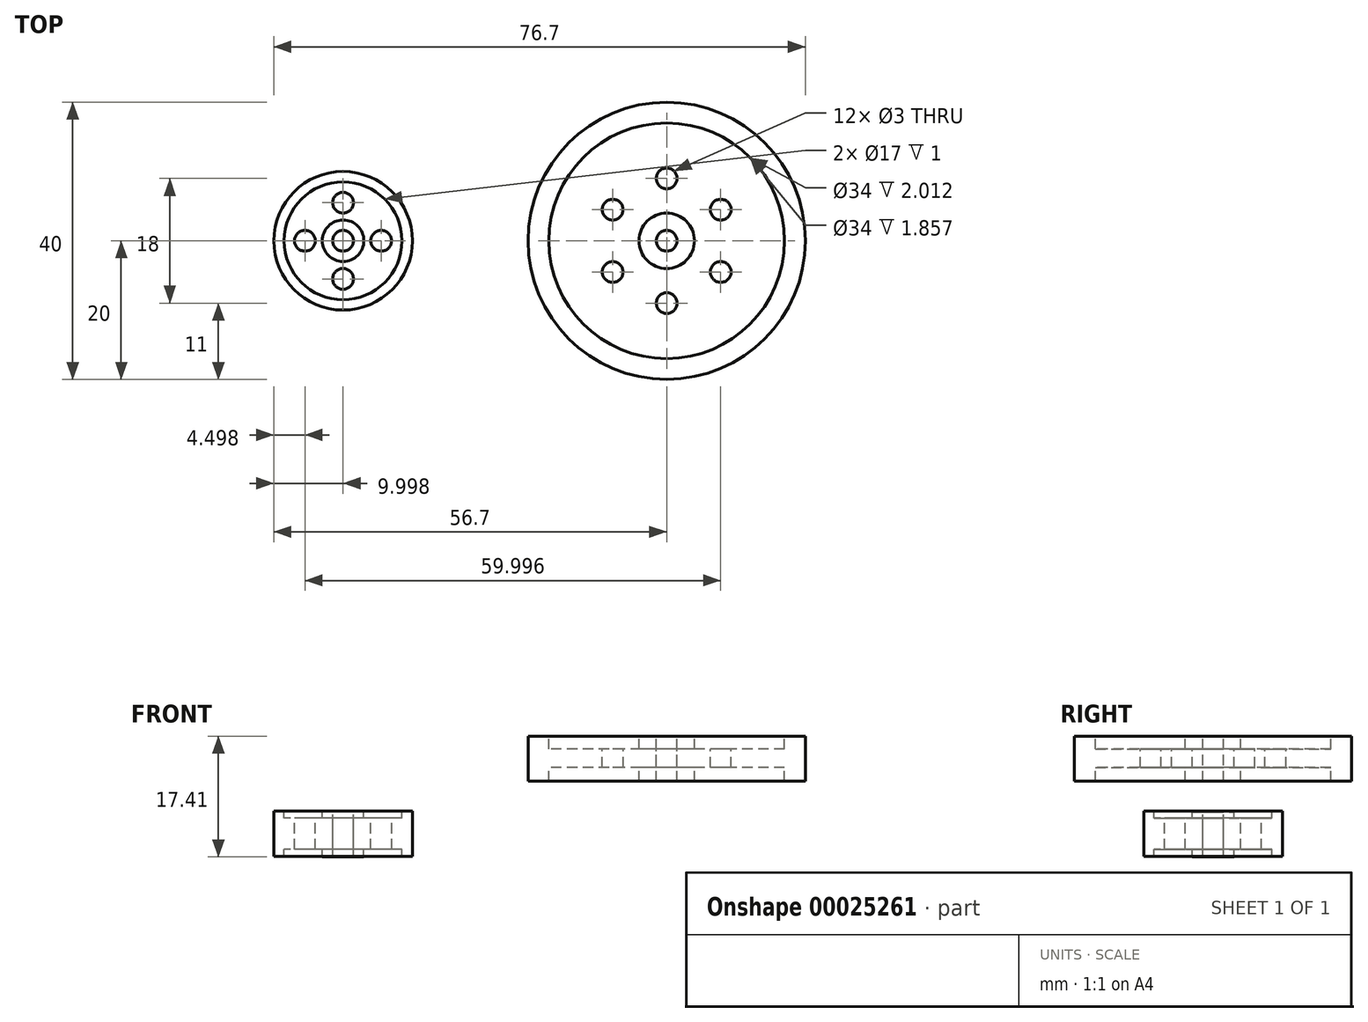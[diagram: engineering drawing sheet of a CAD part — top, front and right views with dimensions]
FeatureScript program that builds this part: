
annotation { "Feature Type Name" : "Feature", "Feature Type Description" : "" }
export const myFeature = defineFeature(function(context is Context, id is Id, definition is map)
    precondition{}
    {
        {
            var Q0;
            Q0=qCreatedBy(makeId("Front.planeOp"),FACE);
            var sketch = newSketch(context, id + "F0", { "sketchPlane" : qUnion([Q0])});
            skLineSegment(sketch, "E0", {"start": v(0, 28.4) * mm, "end": v(0, -27) * mm, "construction": true});
            skLineSegment(sketch, "E1.bottom", {"start": v(1.5, 10.14) * mm, "end": v(4, 10.14) * mm});
            skLineSegment(sketch, "E1.top", {"start": v(1.5, 3.64) * mm, "end": v(4, 3.64) * mm});
            skLineSegment(sketch, "E1.left", {"start": v(1.5, 10.14) * mm, "end": v(1.5, 3.64) * mm});
            skLineSegment(sketch, "E1.right", {"start": v(4, 10.14) * mm, "end": v(4, 3.64) * mm});
            skLineSegment(sketch, "E2.bottom", {"start": v(4, 8.28) * mm, "end": v(17, 8.28) * mm});
            skLineSegment(sketch, "E2.top", {"start": v(4, 5.65) * mm, "end": v(17, 5.65) * mm});
            skLineSegment(sketch, "E2.left", {"start": v(4, 8.28) * mm, "end": v(4, 5.65) * mm});
            skLineSegment(sketch, "E2.right", {"start": v(17, 8.28) * mm, "end": v(17, 5.65) * mm});
            skLineSegment(sketch, "E3.bottom", {"start": v(17, 10.14) * mm, "end": v(20, 10.14) * mm});
            skLineSegment(sketch, "E3.top", {"start": v(17, 3.64) * mm, "end": v(20, 3.64) * mm});
            skLineSegment(sketch, "E3.left", {"start": v(17, 10.14) * mm, "end": v(17, 3.64) * mm});
            skLineSegment(sketch, "E3.right", {"start": v(20, 10.14) * mm, "end": v(20, 3.64) * mm});
            skLineSegment(sketch, "E4", {"start": v(-46.7, 2.05) * mm, "end": v(-46.7, -13.35) * mm, "construction": true});
            skLineSegment(sketch, "E5.bottom", {"start": v(-45.2, -0.77) * mm, "end": v(-43.7, -0.77) * mm});
            skLineSegment(sketch, "E5.top", {"start": v(-45.2, -7.27) * mm, "end": v(-43.7, -7.27) * mm});
            skLineSegment(sketch, "E5.left", {"start": v(-45.2, -0.77) * mm, "end": v(-45.2, -7.27) * mm});
            skLineSegment(sketch, "E5.right", {"start": v(-43.7, -0.77) * mm, "end": v(-43.7, -7.27) * mm});
            skLineSegment(sketch, "E6.bottom", {"start": v(-43.7, -6.19) * mm, "end": v(-38.2, -6.19) * mm});
            skLineSegment(sketch, "E6.top", {"start": v(-43.7, -1.69) * mm, "end": v(-38.2, -1.69) * mm});
            skLineSegment(sketch, "E6.left", {"start": v(-43.7, -1.69) * mm, "end": v(-43.7, -6.19) * mm});
            skLineSegment(sketch, "E6.right", {"start": v(-38.2, -1.69) * mm, "end": v(-38.2, -6.19) * mm});
            skLineSegment(sketch, "E7.bottom", {"start": v(-38.2, -0.69) * mm, "end": v(-36.7, -0.69) * mm});
            skLineSegment(sketch, "E7.top", {"start": v(-38.2, -7.19) * mm, "end": v(-36.7, -7.19) * mm});
            skLineSegment(sketch, "E7.left", {"start": v(-38.2, -0.69) * mm, "end": v(-38.2, -7.19) * mm});
            skLineSegment(sketch, "E7.right", {"start": v(-36.7, -0.69) * mm, "end": v(-36.7, -7.19) * mm});
            skSolve(sketch);
        }
        {
            var Q0;
            {var subQ3=sQuery(id+"F0.wireOp",EDGE,"E1.bottom");Q0=makeQuery(id+"F0.imprint","IMPRINT",FACE,{"disambiguationData":[TD([[makeQuery(id+"F0.imprint","IMPRINT",EDGE,{"derivedFrom":subQ3}),-1.0]])]});}
            var Q1;
            {var subQ4=sQuery(id+"F0.wireOp",EDGE,"E3.bottom");Q1=makeQuery(id+"F0.imprint","IMPRINT",FACE,{"disambiguationData":[TD([[makeQuery(id+"F0.imprint","IMPRINT",EDGE,{"derivedFrom":subQ4}),-1.0]])]});}
            var Q2;
            {var subQ2=sQuery(id+"F0.wireOp",EDGE,"E2.bottom");Q2=makeQuery(id+"F0.imprint","IMPRINT",FACE,{"disambiguationData":[TD([[makeQuery(id+"F0.imprint","IMPRINT",EDGE,{"derivedFrom":subQ2}),-1.0]])]});}
            var Q3;
            Q3=sQuery(id+"F0.wireOp",EDGE,"E0");
            revolve(context, id + "F1", {"entities" : qUnion([Q0, Q1, Q2]), "axis" : qUnion([Q3]), "revolveType" : RevolveType.FULL});
        }
        {
            var Q0;
            Q0=makeQuery(id+"F1.opRevolve","SWEPT_FACE",FACE,{"disambiguationData":[OSD([sQuery(id+"F0.wireOp",EDGE,"E2.bottom")])]});
            var sketch = newSketch(context, id + "F2", { "sketchPlane" : qUnion([Q0])});
            skCircle(sketch, "E8", {"center": v(0, 9) * mm, "radius": 1.5 * mm});
            skCircle(sketch, "E9.1.0", {"center": v(-7.8, 4.5) * mm, "radius": 1.5 * mm});
            skCircle(sketch, "E9.2.0", {"center": v(-7.8, -4.5) * mm, "radius": 1.5 * mm});
            skCircle(sketch, "E9.3.0", {"center": v(0, -9) * mm, "radius": 1.5 * mm});
            skCircle(sketch, "E9.4.0", {"center": v(7.8, -4.5) * mm, "radius": 1.5 * mm});
            skCircle(sketch, "E9.5.0", {"center": v(7.8, 4.5) * mm, "radius": 1.5 * mm});
            skPoint(sketch, "E9.center", {"position": v(0, 0) * mm});
            skSolve(sketch);
        }
        {
            var Q0;
            Q0=sQuery(id+"F2.wireOp",VERTEX,"E8.center");
            var Q1;
            Q1=sQuery(id+"F2.wireOp",VERTEX,"E9.1.0.center");
            var Q2;
            Q2=sQuery(id+"F2.wireOp",VERTEX,"E9.2.0.center");
            var Q3;
            Q3=sQuery(id+"F2.wireOp",VERTEX,"E9.3.0.center");
            var Q4;
            Q4=sQuery(id+"F2.wireOp",VERTEX,"E9.4.0.center");
            var Q5;
            Q5=sQuery(id+"F2.wireOp",VERTEX,"E9.5.0.center");
            var Q6;
            Q6=makeQuery(id+"F1.opRevolve","SWEPT_BODY",BODY,{"disambiguationData":[OSD([sQuery(id+"F0.wireOp",EDGE,"E1.bottom"),sQuery(id+"F0.wireOp",EDGE,"E1.top"),sQuery(id+"F0.wireOp",EDGE,"E1.left"),sQuery(id+"F0.wireOp",EDGE,"E1.right"),sQuery(id+"F0.wireOp",EDGE,"E2.bottom"),sQuery(id+"F0.wireOp",EDGE,"E2.top"),sQuery(id+"F0.wireOp",EDGE,"E3.bottom"),sQuery(id+"F0.wireOp",EDGE,"E3.top"),sQuery(id+"F0.wireOp",EDGE,"E3.left"),sQuery(id+"F0.wireOp",EDGE,"E3.right")])]});
            hole(context, id + "F3", {"style" : HoleStyle.SIMPLE, "holeDiameter" : 3 * mm, "endStyle" : HoleEndStyle.THROUGH, "locations" : qUnion([Q0, Q1, Q2, Q3, Q4, Q5]), "scope" : qUnion([Q6])});
        }
        {
            var Q0;
            {var subQ3=sQuery(id+"F0.wireOp",EDGE,"E5.bottom");Q0=makeQuery(id+"F0.imprint","IMPRINT",FACE,{"disambiguationData":[TD([[makeQuery(id+"F0.imprint","IMPRINT",EDGE,{"derivedFrom":subQ3}),-1.0]])]});}
            var Q1;
            {var subQ2=sQuery(id+"F0.wireOp",EDGE,"E6.bottom");Q1=makeQuery(id+"F0.imprint","IMPRINT",FACE,{"disambiguationData":[TD([[makeQuery(id+"F0.imprint","IMPRINT",EDGE,{"derivedFrom":subQ2}),1.0]])]});}
            var Q2;
            {var subQ3=sQuery(id+"F0.wireOp",EDGE,"E7.bottom");Q2=makeQuery(id+"F0.imprint","IMPRINT",FACE,{"disambiguationData":[TD([[makeQuery(id+"F0.imprint","IMPRINT",EDGE,{"derivedFrom":subQ3}),-1.0]])]});}
            var Q3;
            Q3=sQuery(id+"F0.wireOp",EDGE,"E4");
            revolve(context, id + "F4", {"entities" : qUnion([Q0, Q1, Q2]), "axis" : qUnion([Q3]), "revolveType" : RevolveType.FULL});
        }
        {
            var Q0;
            Q0=makeQuery(id+"F4.opRevolve","SWEPT_FACE",FACE,{"disambiguationData":[OSD([sQuery(id+"F0.wireOp",EDGE,"E6.top")])]});
            var sketch = newSketch(context, id + "F5", { "sketchPlane" : qUnion([Q0])});
            skCircle(sketch, "E10", {"center": v(-46.7, 5.5) * mm, "radius": 1.5 * mm});
            skCircle(sketch, "E11.1.0", {"center": v(-52.2, 0) * mm, "radius": 1.5 * mm});
            skCircle(sketch, "E11.2.0", {"center": v(-46.7, -5.5) * mm, "radius": 1.5 * mm});
            skCircle(sketch, "E11.3.0", {"center": v(-41.2, 0) * mm, "radius": 1.5 * mm});
            skPoint(sketch, "E11.center", {"position": v(-46.7, 0) * mm});
            skSolve(sketch);
        }
        {
            var Q0;
            Q0=sQuery(id+"F5.wireOp",VERTEX,"E11.center");
            var Q1;
            Q1=sQuery(id+"F5.wireOp",VERTEX,"E10.center");
            var Q2;
            Q2=sQuery(id+"F5.wireOp",VERTEX,"E11.3.0.center");
            var Q3;
            Q3=sQuery(id+"F5.wireOp",VERTEX,"E11.2.0.center");
            var Q4;
            Q4=sQuery(id+"F5.wireOp",VERTEX,"E11.1.0.center");
            var Q5;
            Q5=makeQuery(id+"F4.opRevolve","SWEPT_BODY",BODY,{"disambiguationData":[OSD([sQuery(id+"F0.wireOp",EDGE,"E5.bottom"),sQuery(id+"F0.wireOp",EDGE,"E5.top"),sQuery(id+"F0.wireOp",EDGE,"E5.left"),sQuery(id+"F0.wireOp",EDGE,"E5.right"),sQuery(id+"F0.wireOp",EDGE,"E6.bottom"),sQuery(id+"F0.wireOp",EDGE,"E6.top"),sQuery(id+"F0.wireOp",EDGE,"E7.bottom"),sQuery(id+"F0.wireOp",EDGE,"E7.top"),sQuery(id+"F0.wireOp",EDGE,"E7.left"),sQuery(id+"F0.wireOp",EDGE,"E7.right")])]});
            hole(context, id + "F6", {"style" : HoleStyle.SIMPLE, "holeDiameter" : 3 * mm, "endStyle" : HoleEndStyle.THROUGH, "locations" : qUnion([Q0, Q1, Q2, Q3, Q4]), "scope" : qUnion([Q5])});
        }
    });
